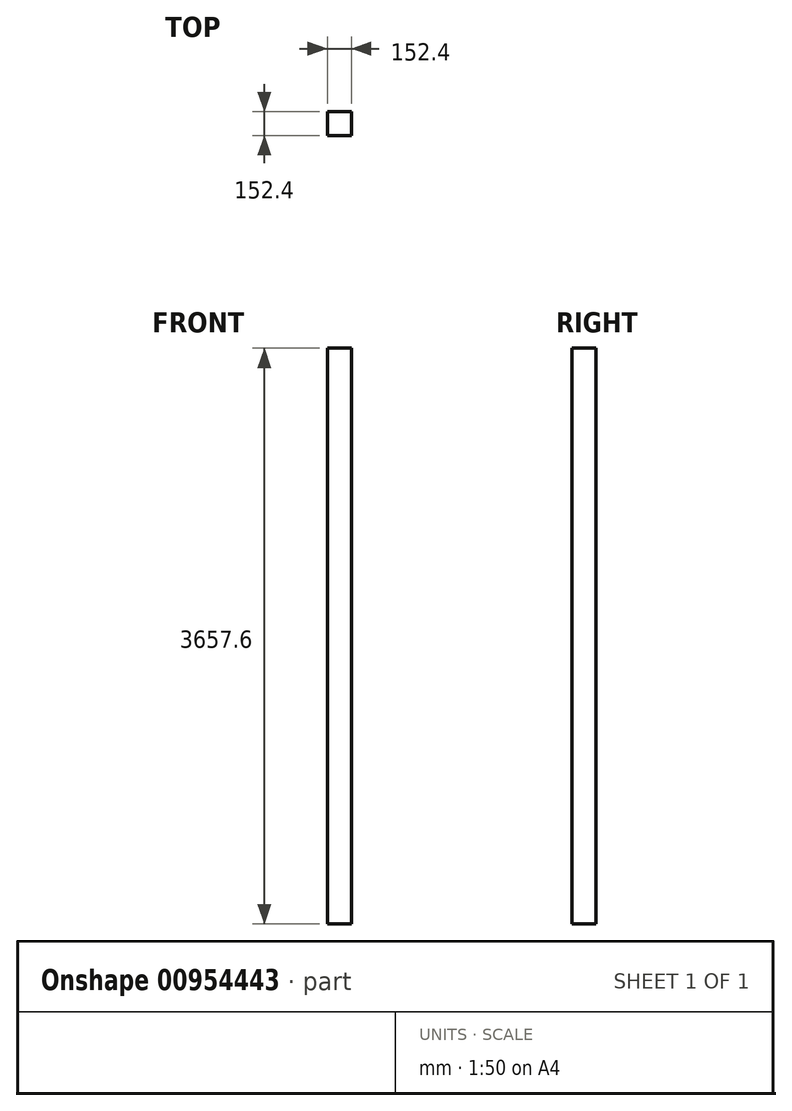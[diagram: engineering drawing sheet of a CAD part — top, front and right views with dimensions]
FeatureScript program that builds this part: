
annotation { "Feature Type Name" : "Feature", "Feature Type Description" : "" }
export const myFeature = defineFeature(function(context is Context, id is Id, definition is map)
    precondition{}
    {
        {
            var Q0;
            Q0=qCreatedBy(makeId("Top.planeOp"),FACE);
            var sketch = newSketch(context, id + "F0", { "sketchPlane" : qUnion([Q0])});
            skLineSegment(sketch, "E0.bottom", {"start": v(0, 0) * mm, "end": v(152.4, 0) * mm});
            skLineSegment(sketch, "E0.top", {"start": v(0, 152.4) * mm, "end": v(152.4, 152.4) * mm});
            skLineSegment(sketch, "E0.left", {"start": v(0, 0) * mm, "end": v(0, 152.4) * mm});
            skLineSegment(sketch, "E0.right", {"start": v(152.4, 0) * mm, "end": v(152.4, 152.4) * mm});
            skSolve(sketch);
        }
        {
            var Q0;
            Q0 = qSketchRegion(id + "F0", true);
            extrude(context, id + "F1", {"entities" : qUnion([Q0]), "depth" : 3657.6 * mm, "offsetDistance" : 25.4 * mm});
        }
    });
